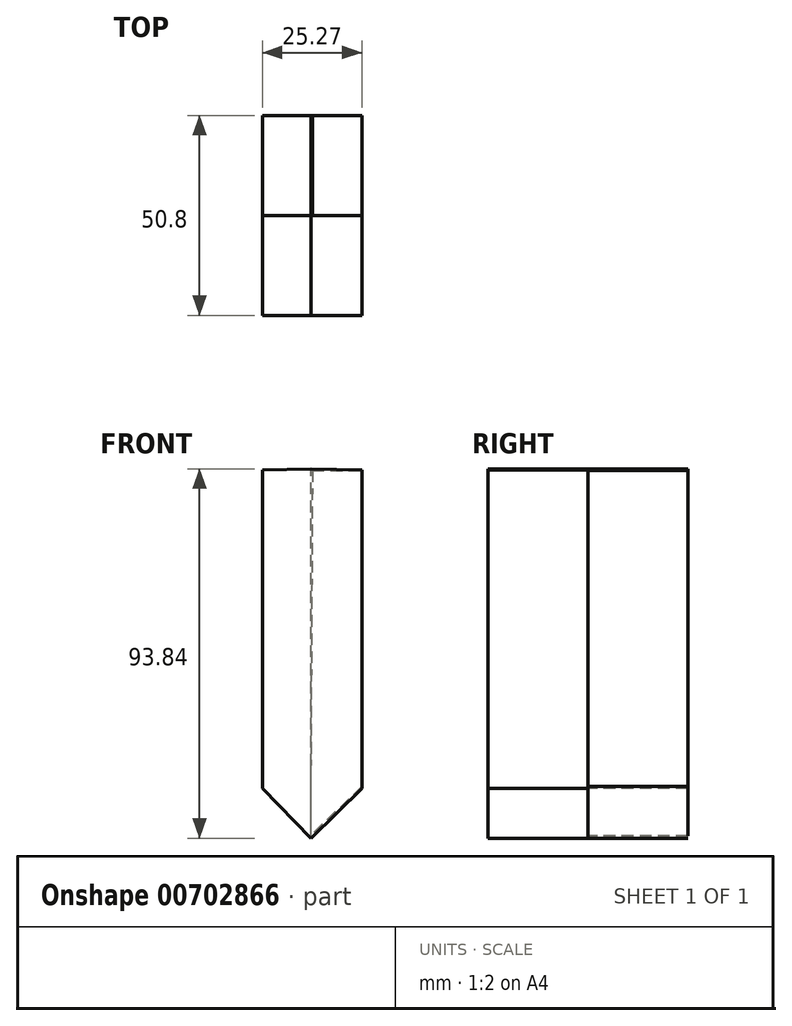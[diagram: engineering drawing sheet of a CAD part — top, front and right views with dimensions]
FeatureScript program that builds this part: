
annotation { "Feature Type Name" : "Feature", "Feature Type Description" : "" }
export const myFeature = defineFeature(function(context is Context, id is Id, definition is map)
    precondition{}
    {
        {
            var Q0;
            Q0=qCreatedBy(makeId("Front.planeOp"),FACE);
            var sketch = newSketch(context, id + "F0", { "sketchPlane" : qUnion([Q0])});
            skLineSegment(sketch, "E0", {"start": v(-25.27, 55.67) * mm, "end": v(-25.27, -25.23) * mm});
            skLineSegment(sketch, "E1", {"start": v(-25.27, -25.23) * mm, "end": v(-12.94, -37.87) * mm});
            skLineSegment(sketch, "E2", {"start": v(-12.94, -37.87) * mm, "end": v(-12.94, 55.97) * mm});
            skLineSegment(sketch, "E3", {"start": v(-12.94, 55.97) * mm, "end": v(-25.27, 55.67) * mm});
            skLineSegment(sketch, "E4", {"start": v(-12.94, -37.87) * mm, "end": v(0, -25.23) * mm});
            skLineSegment(sketch, "E5", {"start": v(0, -25.23) * mm, "end": v(0, 55.67) * mm});
            skLineSegment(sketch, "E6", {"start": v(0, 55.67) * mm, "end": v(-12.94, 55.97) * mm});
            skSolve(sketch);
        }
        {
            var Q0;
            Q0=makeQuery(id+"F0.imprint","IMPRINT",FACE,{"disambiguationData":[TD([[makeQuery(id+"F0.imprint","IMPRINT",EDGE,{"derivedFrom":sQuery(id+"F0.wireOp",EDGE,"E0")}),1.0]])]});
            var Q1;
            Q1=makeQuery(id+"F0.imprint","IMPRINT",FACE,{"disambiguationData":[TD([[makeQuery(id+"F0.imprint","IMPRINT",EDGE,{"derivedFrom":sQuery(id+"F0.wireOp",EDGE,"E2")}),-1.0]])]});
            extrude(context, id + "F1", {"entities" : qUnion([Q0, Q1]), "depth" : 25.4 * mm, "offsetDistance" : 25.4 * mm});
        }
        {
            var Q0;
            Q0=qCreatedBy(makeId("Front.planeOp"),FACE);
            var sketch = newSketch(context, id + "F2", { "sketchPlane" : qUnion([Q0])});
            skLineSegment(sketch, "E7", {"start": v(0, 55.58) * mm, "end": v(0, -24.75) * mm});
            skLineSegment(sketch, "E8", {"start": v(0, -24.75) * mm, "end": v(-13.08, -37.31) * mm});
            skLineSegment(sketch, "E9", {"start": v(-13.08, -37.31) * mm, "end": v(-25.15, -24.75) * mm});
            skLineSegment(sketch, "E10", {"start": v(-25.15, -24.75) * mm, "end": v(-25.15, 55.58) * mm});
            skLineSegment(sketch, "E11", {"start": v(-25.15, 55.58) * mm, "end": v(0, 55.58) * mm});
            skLineSegment(sketch, "E12", {"start": v(-12.57, 55.58) * mm, "end": v(-13.08, -37.31) * mm});
            skSolve(sketch);
        }
        {
            var Q0;
            Q0=makeQuery(id+"F0.imprint","IMPRINT",FACE,{"disambiguationData":[TD([[makeQuery(id+"F0.imprint","IMPRINT",EDGE,{"derivedFrom":sQuery(id+"F0.wireOp",EDGE,"E0")}),1.0]])]});
            var Q1;
            {var subQ0=sQuery(id+"F2.wireOp",EDGE,"E7");Q1=makeQuery(id+"F2.imprint","IMPRINT",FACE,{"disambiguationData":[TD([[makeQuery(id+"F2.imprint","IMPRINT",EDGE,{"derivedFrom":subQ0}),-1.0]])]});}
            extrude(context, id + "F3", {"entities" : qUnion([Q0, Q1]), "oppositeDirection" : true, "depth" : 25.4 * mm, "offsetDistance" : 25.4 * mm});
        }
    });
